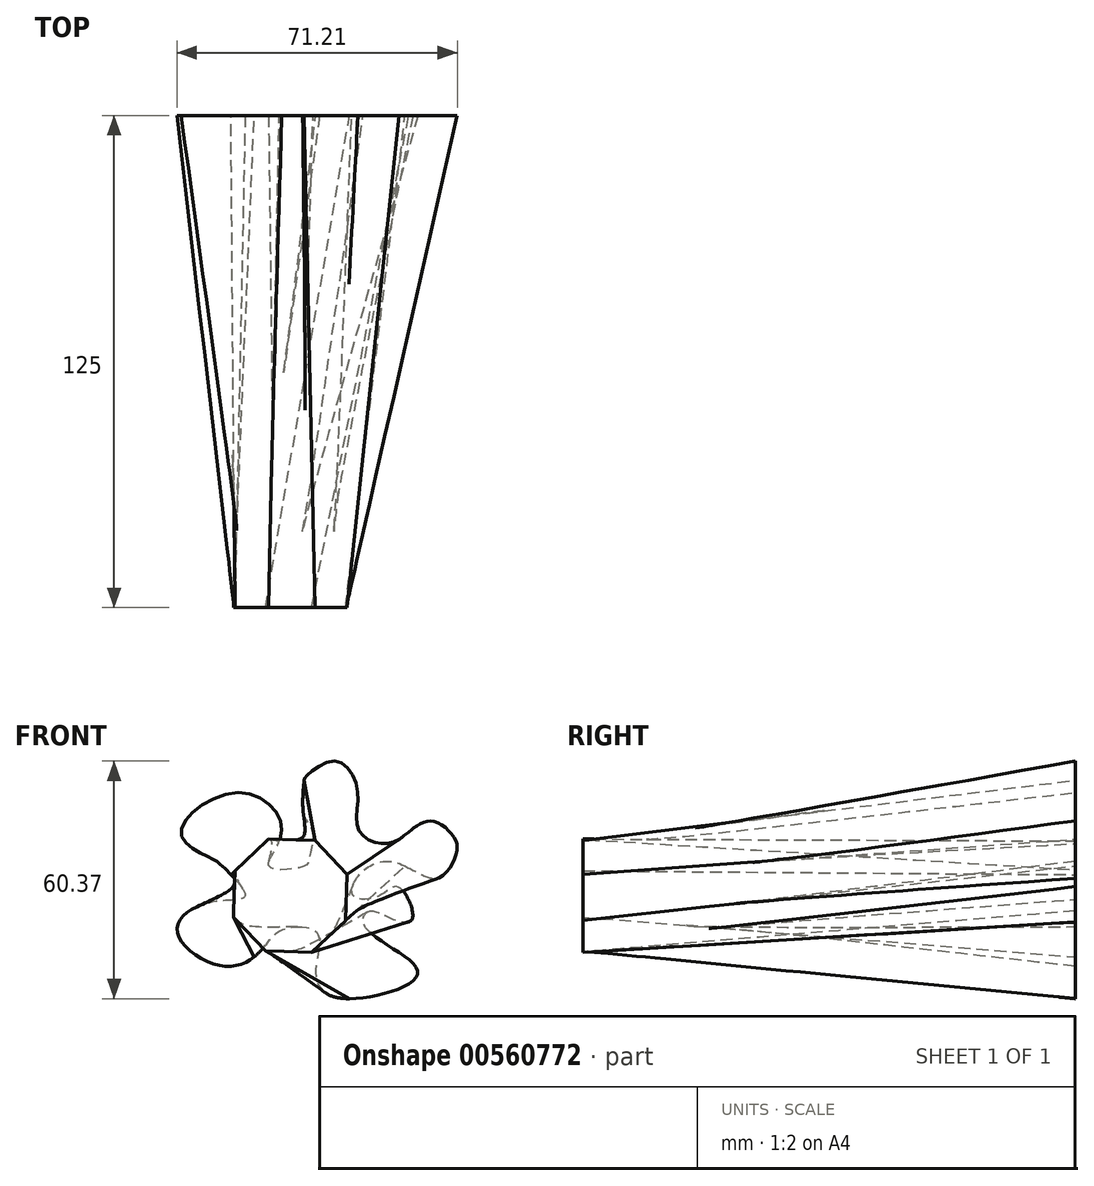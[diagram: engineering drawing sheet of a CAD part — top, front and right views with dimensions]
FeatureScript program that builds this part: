
annotation { "Feature Type Name" : "Feature", "Feature Type Description" : "" }
export const myFeature = defineFeature(function(context is Context, id is Id, definition is map)
    precondition{}
    {
        {
            var Q0;
            Q0=qCreatedBy(makeId("Front.planeOp"),FACE);
            var sketch = newSketch(context, id + "F0", { "sketchPlane" : qUnion([Q0])});
            skFitSpline(sketch, "E0", {"points": [v(-2.16, 16.27) * mm, v(-12.93, 26.2) * mm, v(-27.7, 15.85) * mm, v(-20.1, 9.52) * mm, v(-17.15, 7.4) * mm, v(-11.45, 0) * mm, v(-20.1, -1.67) * mm, v(-28.76, -8.85) * mm, v(-16.73, -17.92) * mm, v(-7.02, -13.5) * mm, v(-1.95, -8.64) * mm, v(6.7, -9.27) * mm, v(6.7, -16.87) * mm, v(7.33, -23) * mm, v(15.14, -26.16) * mm, v(32.45, -19.4) * mm, v(18.94, -7.8) * mm, v(20, -4) * mm, v(25.49, -5.68) * mm, v(30.98, -5.9) * mm, v(27.6, 2.13) * mm, v(22.74, 0) * mm, v(15.99, 0) * mm, v(17.89, 5.72) * mm, v(26.75, 8.46) * mm, v(37.3, 4.45) * mm, v(42.16, 10.57) * mm, v(41.74, 14.58) * mm, v(36.89, 18.8) * mm, v(32.45, 17.96) * mm, v(28.02, 14.58) * mm, v(22.53, 13.32) * mm, v(17.26, 17.11) * mm, v(17.04, 27.25) * mm, v(10.92, 34.21) * mm, v(3.75, 30) * mm, v(3.54, 29.36) * mm, v(3.54, 20.28) * mm, v(5.65, 16.48) * mm, v(4.8, 9.3) * mm, v(3.32, 7.4) * mm, v(-5.33, 7.4) * mm, v(-2.16, 16.27) * mm]});
            skLineSegment(sketch, "E1", {"start": v(-64.22, 25.77) * mm, "end": v(-64.22, 14.8) * mm});
            skLineSegment(sketch, "E2", {"start": v(-72.45, 17.11) * mm, "end": v(-64.22, 25.77) * mm});
            skSolve(sketch);
        }
        {
            var Q0;
            Q0=qCreatedBy(makeId("Front.planeOp"),FACE);
            cPlane(context, id + "F1", {"entities" : qUnion([Q0]), "cplaneType" : CPlaneType.OFFSET, "offset" : 125 * mm, "width" : 150 * mm, "height" : 150 * mm});
        }
        {
            var Q0;
            Q0=qCreatedBy(id+"F1.planeOp",FACE);
            var sketch = newSketch(context, id + "F2", { "sketchPlane" : qUnion([Q0])});
            skCircle(sketch, "E3.cCircle", {"center": v(0, 0) * mm, "radius": 14.24 * mm, "construction": true});
            skLineSegment(sketch, "E3.0", {"start": v(-14.05, 6.32) * mm, "end": v(-5.47, 14.4) * mm});
            skLineSegment(sketch, "E3.1", {"start": v(-5.47, 14.4) * mm, "end": v(6.32, 14.05) * mm});
            skLineSegment(sketch, "E3.2", {"start": v(6.32, 14.05) * mm, "end": v(14.4, 5.47) * mm});
            skLineSegment(sketch, "E3.3", {"start": v(14.4, 5.47) * mm, "end": v(14.05, -6.32) * mm});
            skLineSegment(sketch, "E3.4", {"start": v(14.05, -6.32) * mm, "end": v(5.47, -14.4) * mm});
            skLineSegment(sketch, "E3.5", {"start": v(5.47, -14.4) * mm, "end": v(-6.32, -14.05) * mm});
            skLineSegment(sketch, "E3.6", {"start": v(-6.32, -14.05) * mm, "end": v(-14.4, -5.47) * mm});
            skLineSegment(sketch, "E3.7", {"start": v(-14.4, -5.47) * mm, "end": v(-14.05, 6.32) * mm});
            skPoint(sketch, "E3.0.midPoint", {"position": v(-9.76, 10.36) * mm});
            skSolve(sketch);
        }
        {
            var Q0;
            Q0=makeQuery(id+"F2.imprint","IMPRINT",FACE,{"disambiguationData":[TD([[makeQuery(id+"F2.imprint","IMPRINT",EDGE,{"derivedFrom":sQuery(id+"F2.wireOp",EDGE,"E3.0")}),-1.0]])]});
            var Q1;
            Q1=makeQuery(id+"F0.imprint","IMPRINT",FACE,{"disambiguationData":[TD([[makeQuery(id+"F0.imprint","IMPRINT",EDGE,{"derivedFrom":sQuery(id+"F0.wireOp",EDGE,"E0")}),1.0]])]});
            loft(context, id + "F3", {"sheetProfilesArray" : [{ "sheetProfileEntities" : qUnion([Q0]) }, { "sheetProfileEntities" : qUnion([Q1]) }]});
        }
    });
